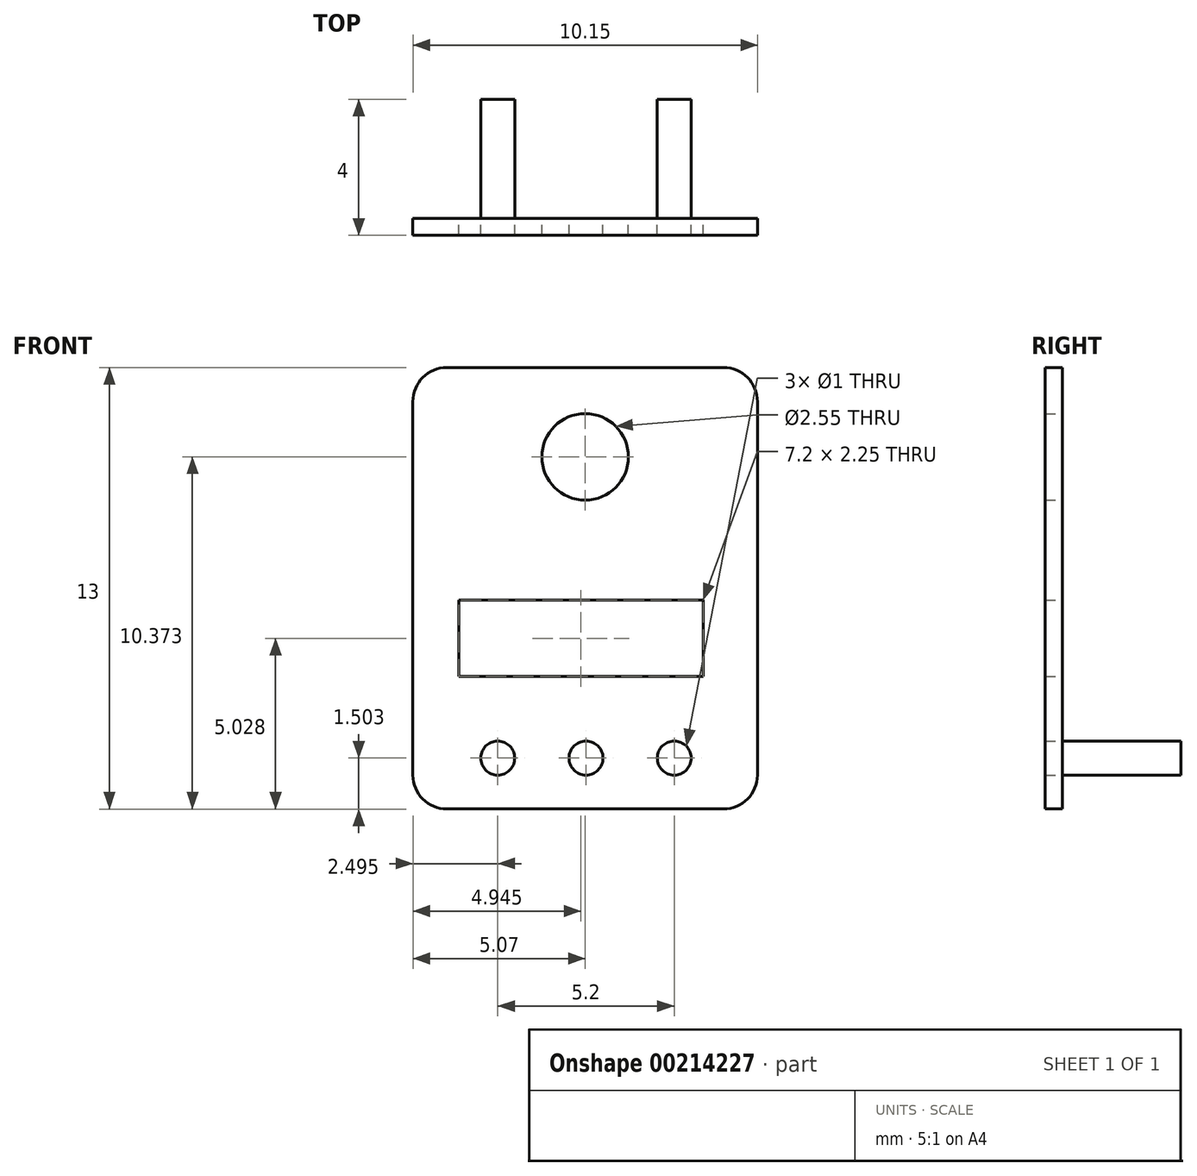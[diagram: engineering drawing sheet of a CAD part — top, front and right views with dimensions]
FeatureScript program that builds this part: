
annotation { "Feature Type Name" : "Feature", "Feature Type Description" : "" }
export const myFeature = defineFeature(function(context is Context, id is Id, definition is map)
    precondition{}
    {
        {
            var Q0;
            Q0=qCreatedBy(makeId("Front.planeOp"),FACE);
            var sketch = newSketch(context, id + "F0", { "sketchPlane" : qUnion([Q0])});
            skLineSegment(sketch, "E0", {"start": v(-15.35, -5.97) * mm, "end": v(-15.35, -16.97) * mm});
            skLineSegment(sketch, "E1", {"start": v(-14.35, -17.97) * mm, "end": v(-6.2, -17.97) * mm});
            skLineSegment(sketch, "E2", {"start": v(-5.2, -16.97) * mm, "end": v(-5.2, -5.97) * mm});
            skLineSegment(sketch, "E3", {"start": v(-6.2, -4.97) * mm, "end": v(-14.35, -4.97) * mm});
            skLineSegment(sketch, "E4", {"start": v(-10.28, -4.97) * mm, "end": v(-10.28, -7.6) * mm, "construction": true});
            skCircle(sketch, "E5", {"center": v(-10.28, -7.6) * mm, "radius": 1.27 * mm});
            skPoint(sketch, "E6.visualSharp", {"position": v(-15.35, -4.97) * mm});
            skArc(sketch, "E6.filletArc", {"start": v(-14.35, -4.97) * mm, "mid": v(-15.06, -5.26) * mm, "end": v(-15.35, -5.97) * mm});
            skPoint(sketch, "E7.visualSharp", {"position": v(-5.2, -4.97) * mm});
            skArc(sketch, "E7.filletArc", {"start": v(-5.2, -5.97) * mm, "mid": v(-5.5, -5.26) * mm, "end": v(-6.2, -4.97) * mm});
            skPoint(sketch, "E8.visualSharp", {"position": v(-5.2, -17.97) * mm});
            skArc(sketch, "E8.filletArc", {"start": v(-6.2, -17.97) * mm, "mid": v(-5.5, -17.67) * mm, "end": v(-5.2, -16.97) * mm});
            skPoint(sketch, "E9.visualSharp", {"position": v(-15.35, -17.97) * mm});
            skArc(sketch, "E9.filletArc", {"start": v(-15.35, -16.97) * mm, "mid": v(-15.06, -17.67) * mm, "end": v(-14.35, -17.97) * mm});
            skLineSegment(sketch, "E10", {"start": v(-7.2, -14.97) * mm, "end": v(-5.2, -14.97) * mm, "construction": true});
            skLineSegment(sketch, "E11", {"start": v(-13.2, -14.97) * mm, "end": v(-15.35, -14.97) * mm, "construction": true});
            skLineSegment(sketch, "E12", {"start": v(-13.2, -14.97) * mm, "end": v(-12.5, -14.97) * mm, "construction": true});
            skLineSegment(sketch, "E13", {"start": v(-12.5, -14.97) * mm, "end": v(-12.5, -17.97) * mm, "construction": true});
            skLineSegment(sketch, "E14", {"start": v(-8, -14.97) * mm, "end": v(-8, -17.97) * mm, "construction": true});
            skLineSegment(sketch, "E15", {"start": v(-12.85, -14.97) * mm, "end": v(-12.85, -17.97) * mm, "construction": true});
            skLineSegment(sketch, "E16", {"start": v(-8, -14.97) * mm, "end": v(-7.65, -14.97) * mm, "construction": true});
            skLineSegment(sketch, "E17", {"start": v(-7.65, -14.97) * mm, "end": v(-7.65, -17.97) * mm, "construction": true});
            skCircle(sketch, "E18", {"center": v(-12.85, -16.47) * mm, "radius": 0.5 * mm});
            skCircle(sketch, "E19", {"center": v(-7.65, -16.47) * mm, "radius": 0.5 * mm});
            skLineSegment(sketch, "E20", {"start": v(-5.2, -17.97) * mm, "end": v(-5.2, -14.07) * mm, "construction": true});
            skLineSegment(sketch, "E21", {"start": v(-5.2, -14.07) * mm, "end": v(-6.8, -14.07) * mm, "construction": true});
            skLineSegment(sketch, "E22", {"start": v(-6.8, -14.07) * mm, "end": v(-14, -14.07) * mm, "construction": true});
            skLineSegment(sketch, "E23", {"start": v(-14, -14.07) * mm, "end": v(-14, -11.82) * mm, "construction": true});
            skLineSegment(sketch, "E24", {"start": v(-14, -11.82) * mm, "end": v(-6.8, -11.82) * mm, "construction": true});
            skLineSegment(sketch, "E25", {"start": v(-6.8, -11.82) * mm, "end": v(-6.8, -14.07) * mm, "construction": true});
            skLineSegment(sketch, "E26", {"start": v(-14, -11.82) * mm, "end": v(-14, -14.07) * mm});
            skLineSegment(sketch, "E27", {"start": v(-14, -14.07) * mm, "end": v(-6.8, -14.07) * mm});
            skLineSegment(sketch, "E28", {"start": v(-6.8, -14.07) * mm, "end": v(-6.8, -11.82) * mm});
            skLineSegment(sketch, "E29", {"start": v(-6.8, -11.82) * mm, "end": v(-14, -11.82) * mm});
            skCircle(sketch, "E30", {"center": v(-10.25, -16.47) * mm, "radius": 0.5 * mm});
            skLineSegment(sketch, "E31", {"start": v(-15.35, -16.47) * mm, "end": v(-5.2, -16.47) * mm, "construction": true});
            skPoint(sketch, "E31.startSnap0", {"position": v(-13.2, -16.47) * mm});
            skSolve(sketch);
        }
        {
            var Q0;
            Q0=makeQuery(id+"F0.imprint","IMPRINT",FACE,{"disambiguationData":[TD([[makeQuery(id+"F0.imprint","IMPRINT",EDGE,{"derivedFrom":sQuery(id+"F0.wireOp",EDGE,"E0")}),1.0]])]});
            extrude(context, id + "F1", {"entities" : qUnion([Q0]), "depth" : 0.5 * mm});
        }
        {
            var Q0;
            {var subQ0=sQuery(id+"F0.wireOp",EDGE,"DZYeYYpx-ez5D-8Xw0-bsWB-ACHPyHD18gHs");var subQ1=sQuery(id+"F0.wireOp",EDGE,"doZjFliG-KwMj-VqZj-TrhQ-weYVOiwAFyRk");var subQ2=makeQuery(id+"F0.imprint","INTERSECT",VERTEX,{"disambiguationData":[OD(0.0)],"derivedFrom":[subQ1,subQ0]});Q0=makeQuery(id+"F0.imprint","IMPRINT",FACE,{"disambiguationData":[TD([[makeQuery(id+"F0.imprint","IMPRINT",EDGE,{"disambiguationData":[TD([[subQ2,-1.0]])],"derivedFrom":subQ1}),-1.0]])]});}
            var Q1;
            {var subQ0=sQuery(id+"F0.wireOp",EDGE,"DZYeYYpx-ez5D-8Xw0-bsWB-ACHPyHD18gHs");var subQ1=sQuery(id+"F0.wireOp",EDGE,"doZjFliG-KwMj-VqZj-TrhQ-weYVOiwAFyRk");var subQ2=makeQuery(id+"F0.imprint","INTERSECT",VERTEX,{"disambiguationData":[OD(0.0)],"derivedFrom":[subQ1,subQ0]});Q1=makeQuery(id+"F0.imprint","IMPRINT",FACE,{"disambiguationData":[TD([[makeQuery(id+"F0.imprint","IMPRINT",EDGE,{"disambiguationData":[TD([[subQ2,-1.0]])],"derivedFrom":subQ1}),1.0]])]});}
            var Q2;
            Q2=makeQuery(id+"F0.imprint","IMPRINT",FACE,{"disambiguationData":[TD([[makeQuery(id+"F0.imprint","IMPRINT",EDGE,{"derivedFrom":sQuery(id+"F0.wireOp",EDGE,"E18")}),1.0]])]});
            var Q3;
            Q3=makeQuery(id+"F0.imprint","IMPRINT",FACE,{"disambiguationData":[TD([[makeQuery(id+"F0.imprint","IMPRINT",EDGE,{"derivedFrom":sQuery(id+"F0.wireOp",EDGE,"E19")}),1.0]])]});
            extrude(context, id + "F2", {"entities" : qUnion([Q0, Q1, Q2, Q3]), "oppositeDirection" : true, "depth" : 3.5 * mm});
        }
        {
            var Q0;
            Q0=makeQuery(id+"F0.imprint","IMPRINT",FACE,{"disambiguationData":[TD([[makeQuery(id+"F0.imprint","IMPRINT",EDGE,{"derivedFrom":sQuery(id+"F0.wireOp",EDGE,"E26")}),1.0]])]});
            extrude(context, id + "F3", {"entities" : qUnion([Q0]), "operationType" : NewBodyOperationType.REMOVE, "oppositeDirection" : true, "depth" : 1 * mm});
        }
    });
